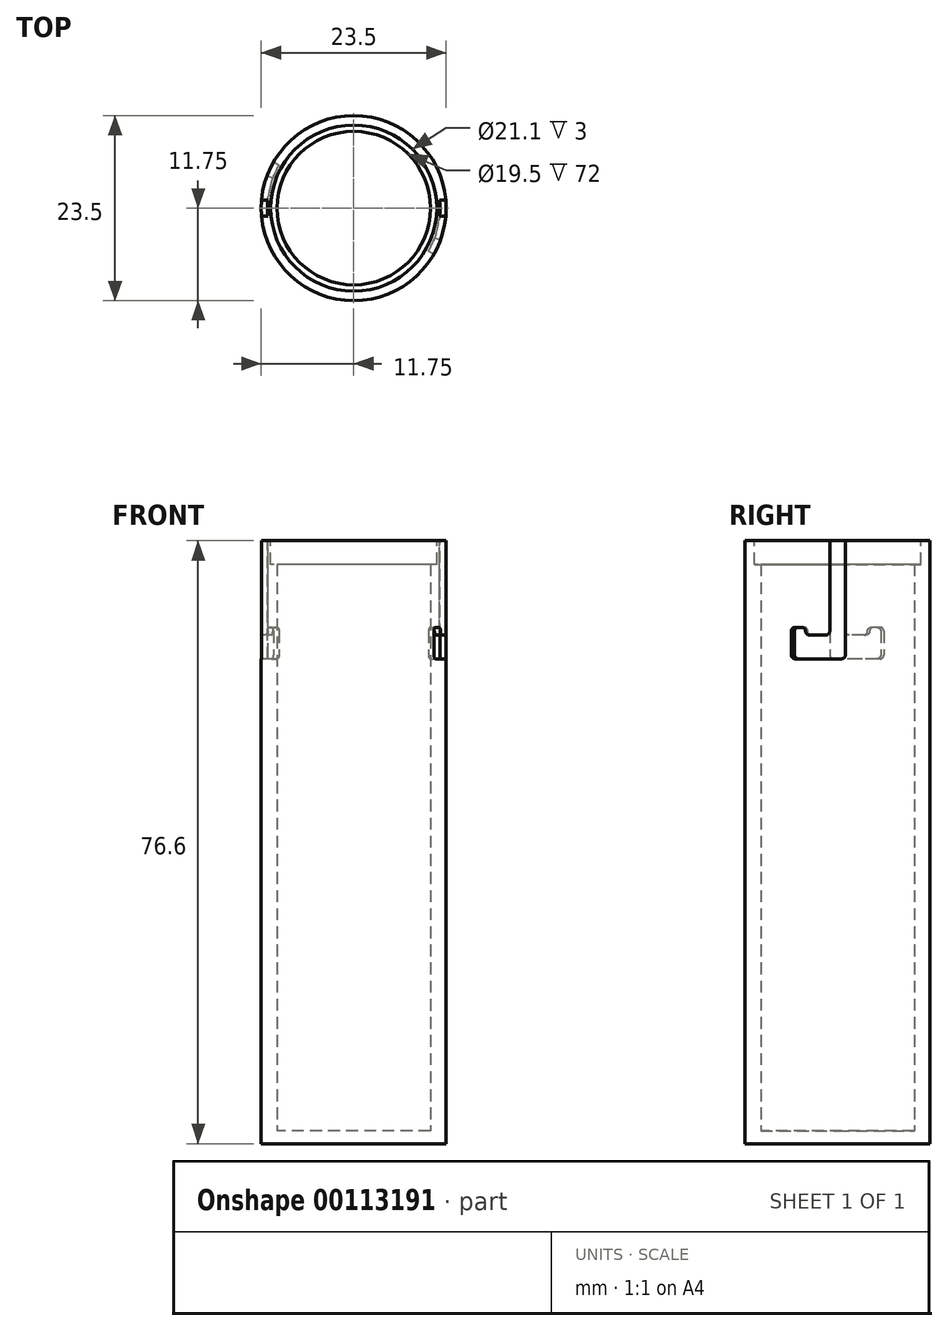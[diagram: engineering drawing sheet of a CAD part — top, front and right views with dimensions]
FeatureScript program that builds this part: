
annotation { "Feature Type Name" : "Feature", "Feature Type Description" : "" }
export const myFeature = defineFeature(function(context is Context, id is Id, definition is map)
    precondition{}
    {
        {
            var Q0;
            Q0=qCreatedBy(makeId("Top.planeOp"),FACE);
            var sketch = newSketch(context, id + "F0", { "sketchPlane" : qUnion([Q0])});
            skCircle(sketch, "E0", {"center": v(0, 0) * mm, "radius": 9.75 * mm});
            skCircle(sketch, "E1.0", {"center": v(0, 0) * mm, "radius": 11.75 * mm});
            skSolve(sketch);
        }
        {
            var Q0;
            Q0 = qSketchRegion(id + "F0", true);
            extrude(context, id + "F1", {"entities" : qUnion([Q0]), "depth" : 75 * mm});
        }
        {
            var Q0;
            Q0=makeQuery(id+"F0.imprint","IMPRINT",FACE,{"disambiguationData":[TD([[makeQuery(id+"F0.imprint","IMPRINT",EDGE,{"derivedFrom":sQuery(id+"F0.wireOp",EDGE,"E0")}),-1.0]])]});
            var Q1;
            Q1=makeQuery(id+"F0.imprint","IMPRINT",FACE,{"disambiguationData":[TD([[makeQuery(id+"F0.imprint","IMPRINT",EDGE,{"derivedFrom":sQuery(id+"F0.wireOp",EDGE,"E0")}),1.0]])]});
            extrude(context, id + "F2", {"entities" : qUnion([Q0, Q1]), "operationType" : NewBodyOperationType.ADD, "oppositeDirection" : true, "depth" : 1.6 * mm});
        }
        {
            var Q0;
            Q0=makeQuery(id+"F1.opExtrude","CAP_FACE",FACE,{"disambiguationData":[OSD([sQuery(id+"F0.wireOp",EDGE,"E0"),sQuery(id+"F0.wireOp",EDGE,"E1.0")])],"isStart":false});
            var sketch = newSketch(context, id + "F3", { "sketchPlane" : qUnion([Q0])});
            skCircle(sketch, "E2.0", {"center": v(0, 0) * mm, "radius": 11.75 * mm});
            skCircle(sketch, "E3.0", {"center": v(0, 0) * mm, "radius": 10.95 * mm});
            skSolve(sketch);
        }
        {
            var Q0;
            Q0=makeQuery(id+"F1.opExtrude","CAP_FACE",FACE,{"disambiguationData":[OSD([sQuery(id+"F0.wireOp",EDGE,"E0"),sQuery(id+"F0.wireOp",EDGE,"E1.0")])],"isStart":false});
            var sketch = newSketch(context, id + "F4", { "sketchPlane" : qUnion([Q0])});
            skLineSegment(sketch, "E4", {"start": v(-11.75, 0) * mm, "end": v(11.75, 0) * mm, "construction": true});
            skLineSegment(sketch, "E5", {"start": v(-11.75, 1) * mm, "end": v(-11.75, -1) * mm});
            skLineSegment(sketch, "E6", {"start": v(-11.75, 1) * mm, "end": v(-10.9, 1) * mm});
            skLineSegment(sketch, "E7", {"start": v(-10.9, -1) * mm, "end": v(-11.75, -1) * mm});
            skLineSegment(sketch, "E8", {"start": v(0, 0) * mm, "end": v(0, 3.72) * mm, "construction": true});
            skPoint(sketch, "E8.endSnap0", {"position": v(0, 0) * mm});
            skLineSegment(sketch, "E9.MirrorCS", {"start": v(10.9, -1) * mm, "end": v(11.75, -1) * mm});
            skLineSegment(sketch, "E10.MirrorCS", {"start": v(11.75, 1) * mm, "end": v(10.9, 1) * mm});
            skLineSegment(sketch, "E11.MirrorCS", {"start": v(11.75, 1) * mm, "end": v(11.75, -1) * mm});
            skArc(sketch, "E12.trimOffspring", {"start": v(10.9, -1) * mm, "mid": v(10.95, 0) * mm, "end": v(10.9, 1) * mm});
            skArc(sketch, "E13.0", {"start": v(-10.9, 1) * mm, "mid": v(-10.95, 0) * mm, "end": v(-10.9, -1) * mm});
            skSolve(sketch);
        }
        {
            var Q0;
            Q0 = qSketchRegion(id + "F4", true);
            extrude(context, id + "F5", {"entities" : qUnion([Q0]), "operationType" : NewBodyOperationType.REMOVE, "oppositeDirection" : true, "depth" : 15 * mm});
        }
        {
            var Q0;
            Q0=makeQuery(id+"F5.boolean.opBoolean","COPY",FACE,{"derivedFrom":makeQuery(id+"F5.opExtrude","CAP_FACE",FACE,{"disambiguationData":[OSD([sQuery(id+"F4.wireOp",EDGE,"E5"),sQuery(id+"F4.wireOp",EDGE,"E6"),sQuery(id+"F4.wireOp",EDGE,"K4f3YTJh-ZCxw-JD0R-Xchg-HOlw2ML41x80"),sQuery(id+"F4.wireOp",EDGE,"E7")])],"isStart":false})});
            var sketch = newSketch(context, id + "F6", { "sketchPlane" : qUnion([Q0])});
            skLineSegment(sketch, "E14", {"start": v(0, 0) * mm, "end": v(4.78, 0) * mm, "construction": true});
            skArc(sketch, "E15.0", {"start": v(-10.18, 5.88) * mm, "mid": v(-11.47, 2.55) * mm, "end": v(-11.7, -1) * mm});
            skArc(sketch, "E15.1", {"start": v(-9.48, 5.47) * mm, "mid": v(-10.7, 2.35) * mm, "end": v(-10.9, -1) * mm});
            skLineSegment(sketch, "E16", {"start": v(-10.18, 5.88) * mm, "end": v(-9.48, 5.48) * mm});
            skLineSegment(sketch, "E17", {"start": v(-9.48, 5.48) * mm, "end": v(9.48, -5.48) * mm, "construction": true});
            skLineSegment(sketch, "E18", {"start": v(9.48, -5.48) * mm, "end": v(10.18, -5.88) * mm});
            skLineSegment(sketch, "E19.0", {"start": v(-10.9, -1) * mm, "end": v(-11.7, -1) * mm});
            skLineSegment(sketch, "E20.0", {"start": v(11.7, 1) * mm, "end": v(10.9, 1) * mm});
            skArc(sketch, "E21.trimOffspring", {"start": v(9.48, -5.48) * mm, "mid": v(10.7, -2.35) * mm, "end": v(10.9, 1) * mm});
            skArc(sketch, "E22.trimOffspring", {"start": v(10.18, -5.88) * mm, "mid": v(11.47, -2.55) * mm, "end": v(11.7, 1) * mm});
            skSolve(sketch);
        }
        {
            var Q0;
            Q0 = qSketchRegion(id + "F6", true);
            extrude(context, id + "F7", {"entities" : qUnion([Q0]), "operationType" : NewBodyOperationType.REMOVE, "depth" : 3 * mm});
        }
        {
            var Q0;
            Q0=makeQuery(id+"F7.boolean.opBoolean","MERGE",FACE,{"derivedFrom":[makeQuery(id+"F5.boolean.opBoolean","COPY",FACE,{"derivedFrom":makeQuery(id+"F5.opExtrude","CAP_FACE",FACE,{"disambiguationData":[OSD([sQuery(id+"F4.wireOp",EDGE,"E5"),sQuery(id+"F4.wireOp",EDGE,"E6"),sQuery(id+"F4.wireOp",EDGE,"E7"),sQuery(id+"F4.wireOp",EDGE,"E13.0")])],"isStart":false})}),makeQuery(id+"F7.opExtrude","CAP_FACE",FACE,{"disambiguationData":[OSD([sQuery(id+"F6.wireOp",EDGE,"E15.0"),sQuery(id+"F6.wireOp",EDGE,"E15.1"),sQuery(id+"F6.wireOp",EDGE,"E16"),sQuery(id+"F6.wireOp",EDGE,"E19.0")])],"isStart":true})]});
            var sketch = newSketch(context, id + "F8", { "sketchPlane" : qUnion([Q0])});
            skLineSegment(sketch, "E23.0", {"start": v(-10.18, 5.88) * mm, "end": v(-9.48, 5.48) * mm});
            skLineSegment(sketch, "E23.1", {"start": v(9.48, -5.48) * mm, "end": v(10.18, -5.88) * mm});
            skArc(sketch, "E24.0", {"start": v(-10.18, 5.88) * mm, "mid": v(-10.64, 4.99) * mm, "end": v(-11.02, 4.06) * mm});
            skArc(sketch, "E24.1", {"start": v(-9.48, 5.47) * mm, "mid": v(-9.91, 4.65) * mm, "end": v(-10.27, 3.79) * mm});
            skArc(sketch, "E24.2", {"start": v(9.48, -5.48) * mm, "mid": v(9.91, -4.65) * mm, "end": v(10.27, -3.79) * mm});
            skArc(sketch, "E24.3", {"start": v(10.18, -5.88) * mm, "mid": v(10.64, -4.99) * mm, "end": v(11.02, -4.06) * mm});
            skLineSegment(sketch, "E25", {"start": v(-11.02, 4.06) * mm, "end": v(-10.27, 3.79) * mm});
            skLineSegment(sketch, "E26", {"start": v(10.27, -3.79) * mm, "end": v(11.02, -4.06) * mm});
            skLineSegment(sketch, "E27", {"start": v(-10.27, 3.79) * mm, "end": v(10.27, -3.79) * mm, "construction": true});
            skSolve(sketch);
        }
        {
            var Q0;
            Q0 = qSketchRegion(id + "F8", true);
            extrude(context, id + "F9", {"entities" : qUnion([Q0]), "operationType" : NewBodyOperationType.REMOVE, "depth" : 4 * mm});
        }
        {
            var Q0;
            Q0=makeQuery(id+"F9.boolean.opBoolean","INTERSECT",EDGE,{"derivedFrom":[makeQuery(id+"F7.boolean.opBoolean","COPY",FACE,{"derivedFrom":makeQuery(id+"F7.opExtrude","CAP_FACE",FACE,{"disambiguationData":[OSD([sQuery(id+"F6.wireOp",EDGE,"E15.0"),sQuery(id+"F6.wireOp",EDGE,"E15.1"),sQuery(id+"F6.wireOp",EDGE,"E16"),sQuery(id+"F6.wireOp",EDGE,"E19.0")])],"isStart":false})}),makeQuery(id+"F9.opExtrude","SWEPT_FACE",FACE,{"disambiguationData":[OSD([sQuery(id+"F8.wireOp",EDGE,"E25")])]})]});
            var Q1;
            Q1=makeQuery(id+"F9.boolean.opBoolean","COPY",EDGE,{"derivedFrom":makeQuery(id+"F9.opExtrude","CAP_EDGE",EDGE,{"disambiguationData":[OSD([sQuery(id+"F8.wireOp",EDGE,"E25")])],"isStart":false})});
            var Q2;
            Q2=makeQuery(id+"F9.boolean.opBoolean","COPY",EDGE,{"derivedFrom":makeQuery(id+"F9.opExtrude","CAP_EDGE",EDGE,{"disambiguationData":[OSD([sQuery(id+"F8.wireOp",EDGE,"E23.0")])],"isStart":false})});
            var Q3;
            Q3=makeQuery(id+"F7.boolean.opBoolean","COPY",EDGE,{"derivedFrom":makeQuery(id+"F7.opExtrude","CAP_EDGE",EDGE,{"disambiguationData":[OSD([sQuery(id+"F6.wireOp",EDGE,"E16")])],"isStart":true})});
            var Q4;
            Q4=makeQuery(id+"F5.boolean.opBoolean","COPY",EDGE,{"derivedFrom":makeQuery(id+"F5.opExtrude","CAP_EDGE",EDGE,{"disambiguationData":[OSD([sQuery(id+"F4.wireOp",EDGE,"E7")])],"isStart":false})});
            var Q5;
            Q5=makeQuery(id+"F7.boolean.opBoolean","INTERSECT",EDGE,{"derivedFrom":[makeQuery(id+"F5.boolean.opBoolean","COPY",FACE,{"derivedFrom":makeQuery(id+"F5.opExtrude","SWEPT_FACE",FACE,{"disambiguationData":[OSD([sQuery(id+"F4.wireOp",EDGE,"E6")])]})}),makeQuery(id+"F7.opExtrude","CAP_FACE",FACE,{"disambiguationData":[OSD([sQuery(id+"F6.wireOp",EDGE,"E15.0"),sQuery(id+"F6.wireOp",EDGE,"E15.1"),sQuery(id+"F6.wireOp",EDGE,"E16"),sQuery(id+"F6.wireOp",EDGE,"E19.0")])],"isStart":false})]});
            var Q6;
            Q6=makeQuery(id+"F5.boolean.opBoolean","COPY",EDGE,{"derivedFrom":makeQuery(id+"F5.opExtrude","CAP_EDGE",EDGE,{"disambiguationData":[OSD([sQuery(id+"F4.wireOp",EDGE,"E10.MirrorCS")])],"isStart":false})});
            var Q7;
            Q7=makeQuery(id+"F7.boolean.opBoolean","INTERSECT",EDGE,{"derivedFrom":[makeQuery(id+"F5.boolean.opBoolean","COPY",FACE,{"derivedFrom":makeQuery(id+"F5.opExtrude","SWEPT_FACE",FACE,{"disambiguationData":[OSD([sQuery(id+"F4.wireOp",EDGE,"E9.MirrorCS")])]})}),makeQuery(id+"F7.opExtrude","CAP_FACE",FACE,{"disambiguationData":[OSD([sQuery(id+"F6.wireOp",EDGE,"E18"),sQuery(id+"F6.wireOp",EDGE,"E20.0"),sQuery(id+"F6.wireOp",EDGE,"E21.trimOffspring"),sQuery(id+"F6.wireOp",EDGE,"E22.trimOffspring")])],"isStart":false})]});
            var Q8;
            Q8=makeQuery(id+"F9.boolean.opBoolean","COPY",EDGE,{"derivedFrom":makeQuery(id+"F9.opExtrude","CAP_EDGE",EDGE,{"disambiguationData":[OSD([sQuery(id+"F8.wireOp",EDGE,"E23.1")])],"isStart":false})});
            var Q9;
            Q9=makeQuery(id+"F9.boolean.opBoolean","INTERSECT",EDGE,{"derivedFrom":[makeQuery(id+"F7.boolean.opBoolean","COPY",FACE,{"derivedFrom":makeQuery(id+"F7.opExtrude","CAP_FACE",FACE,{"disambiguationData":[OSD([sQuery(id+"F6.wireOp",EDGE,"E18"),sQuery(id+"F6.wireOp",EDGE,"E20.0"),sQuery(id+"F6.wireOp",EDGE,"E21.trimOffspring"),sQuery(id+"F6.wireOp",EDGE,"E22.trimOffspring")])],"isStart":false})}),makeQuery(id+"F9.opExtrude","SWEPT_FACE",FACE,{"disambiguationData":[OSD([sQuery(id+"F8.wireOp",EDGE,"E26")])]})]});
            var Q10;
            Q10=makeQuery(id+"F9.boolean.opBoolean","COPY",EDGE,{"derivedFrom":makeQuery(id+"F9.opExtrude","CAP_EDGE",EDGE,{"disambiguationData":[OSD([sQuery(id+"F8.wireOp",EDGE,"E26")])],"isStart":false})});
            var Q11;
            Q11=makeQuery(id+"F7.boolean.opBoolean","COPY",EDGE,{"derivedFrom":makeQuery(id+"F7.opExtrude","CAP_EDGE",EDGE,{"disambiguationData":[OSD([sQuery(id+"F6.wireOp",EDGE,"E18")])],"isStart":true})});
            fillet(context, id + "F10", {"entities" : qUnion([Q0, Q1, Q2, Q3, Q4, Q5, Q6, Q7, Q8, Q9, Q10, Q11]), "radius" : .5 * mm, "tangentPropagation" : true, "allowEdgeOverflow" : false});
        }
        {
            var Q0;
            Q0=makeQuery(id+"F3.imprint","IMPRINT",FACE,{"disambiguationData":[TD([[makeQuery(id+"F3.imprint","IMPRINT",EDGE,{"derivedFrom":sQuery(id+"F3.wireOp",EDGE,"E3.0")}),1.0]])]});
            var sketch = newSketch(context, id + "F11", { "sketchPlane" : qUnion([Q0])});
            skCircle(sketch, "E28.0", {"center": v(0, 0) * mm, "radius": 10.55 * mm});
            skSolve(sketch);
        }
        {
            var Q0;
            Q0 = qSketchRegion(id + "F11", true);
            extrude(context, id + "F12", {"entities" : qUnion([Q0]), "operationType" : NewBodyOperationType.REMOVE, "oppositeDirection" : true, "depth" : 3 * mm});
        }
        {
            var Q0;
            Q0=makeQuery(id+"F2.opExtrude","CAP_FACE",FACE,{"disambiguationData":[OSD([sQuery(id+"F0.wireOp",EDGE,"E1.0")])],"isStart":false});
            var Q1;
            Q1=makeQuery(id+"F1.opExtrude","CAP_FACE",FACE,{"disambiguationData":[OSD([sQuery(id+"F0.wireOp",EDGE,"E0"),sQuery(id+"F0.wireOp",EDGE,"E1.0")])],"isStart":false});
            cPlane(context, id + "F13", {"entities" : qUnion([Q0, Q1]), "cplaneType" : CPlaneType.MID_PLANE, "offset" : 25 * mm, "width" : 150 * mm, "height" : 150 * mm});
        }
        {
            var Q0;
            Q0=qCreatedBy(makeId("Right.planeOp"),FACE);
            var sketch = newSketch(context, id + "F14", { "sketchPlane" : qUnion([Q0])});
            skCircle(sketch, "E29", {"center": v(0, 36.7) * mm, "radius": 38.3 * mm, "construction": true});
            skSolve(sketch);
        }
        {
            var Q0;
            Q0=qCreatedBy(id+"F13.planeOp",FACE);
            var sketch = newSketch(context, id + "F15", { "sketchPlane" : qUnion([Q0])});
            skLineSegment(sketch, "E30", {"start": v(16.25, 0) * mm, "end": v(-16.25, 0) * mm, "construction": true});
            skSolve(sketch);
        }
    });
